# Revit family: Electrical-Box_FSR_T3AC2-CP
name_source: partatom
category: Electrical Fixtures
units: mm (PartAtom-declared; Revit-internal decimal feet)

## family parameters
Always vertical = No
Classification Number = 23.85.10.17.11
Cut with Voids When Loaded = No
Maintain Annotation Orientation = No
Part Type = Normal
Room Calculation Point = No
Round Connector Dimension = Use Diameter
Shared = No
Work Plane-Based = Yes

## types (1)
- 2008_Generic Model
    Assembly Code = D5020100
    Body Material = Material and Finish as Specified in 26 27 26
    Construction Details = ftp://doclib.fsrinc.com/
    Cover Material = Material and Finish as Specified in 26 27 26
    Default Elevation = 48"
    Description = Electrical Box as Specified in 26 27 26
    Device 1 = Device : AC Power Outlet
    Device 2 = Device : AC Power Outlet
    Device 3 = Device : Keystone As Specified
    Device 4 = Device : Keystone As Specified
    Device 5 = Device : None
    Device 6 = Device : None
    Device Finish = Jack - As Specified
    Expected Lifespan (Years) = 0
    Green Building-LEED = http://www.arcat.com
    Installation_Fabricaton = ftp://doclib.fsrinc.com/
    Keynote = 26 27 26
    Maintenance Schedule (Months) = 0
    Manufacturer = FSR Inc.
    Manufacturer Fax = 973-785-4207
    Manufacturer Website = http://www.fsrinc.com
    Model = As Specified in 26 27 26
    Product Data = http://www.arcat.com
    Sales Information = http://www.fsrinc.com
    Send Message = http://admin.arcat.com
    Specification = http://www.arcat.com
    Test Data = ftp://doclib.fsrinc.com/
    URL = http://www.fsrinc.com
    Warranty Duration (Years) = 0

## geometry (parser evidence)
native form markers: Blend x40, Sweep x6
no freeform markers — native parametric forms only
